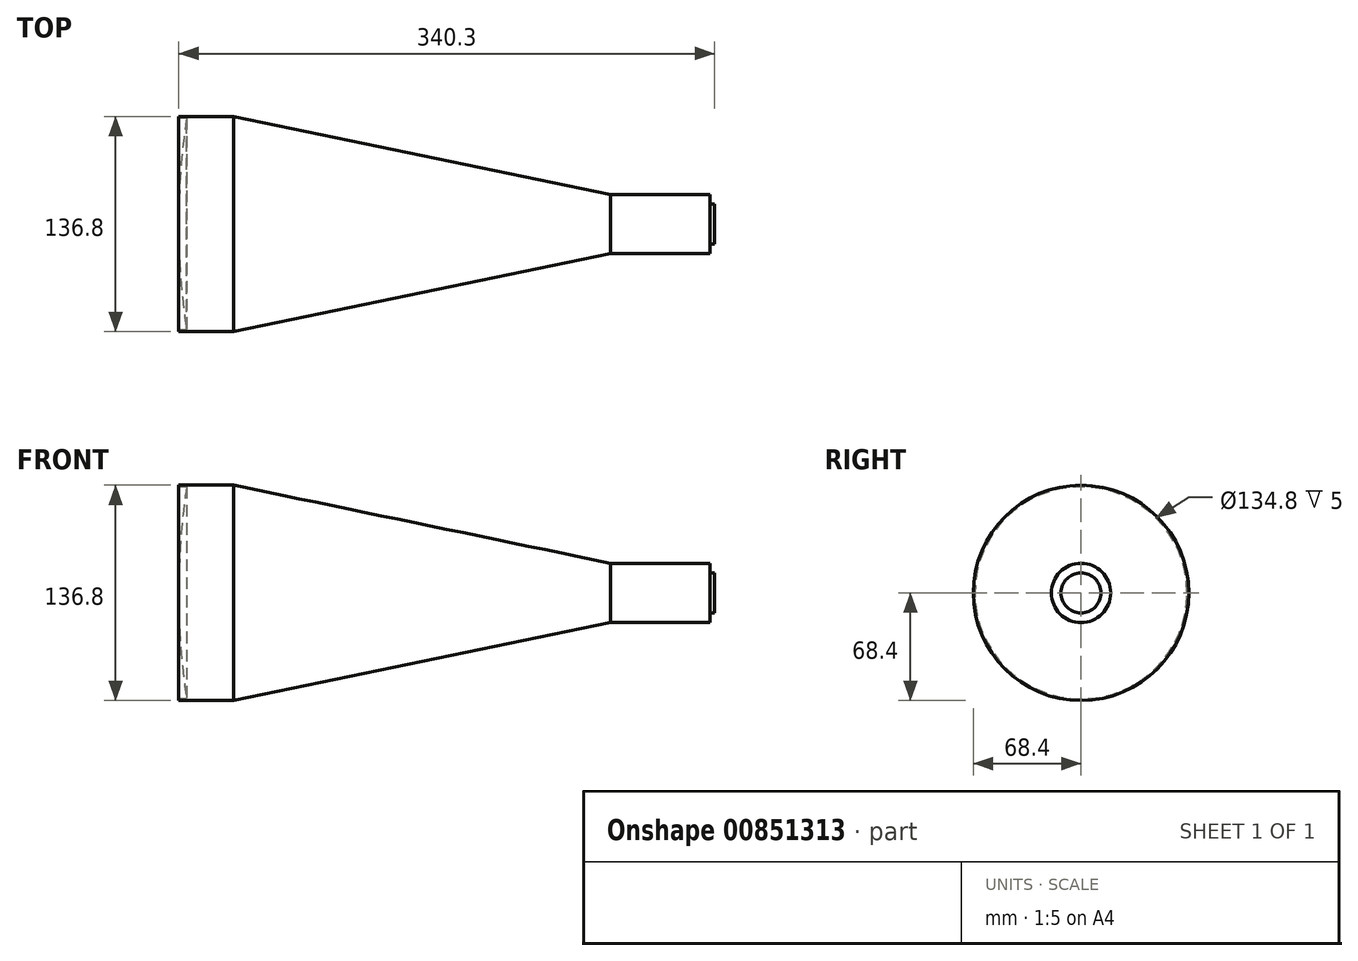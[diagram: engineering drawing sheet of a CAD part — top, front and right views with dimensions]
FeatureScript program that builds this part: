
annotation { "Feature Type Name" : "Feature", "Feature Type Description" : "" }
export const myFeature = defineFeature(function(context is Context, id is Id, definition is map)
    precondition{}
    {
        {
            var Q0;
            Q0=qCreatedBy(makeId("Front.planeOp"),FACE);
            var sketch = newSketch(context, id + "F0", { "sketchPlane" : qUnion([Q0])});
            skLineSegment(sketch, "E0", {"start": v(0, 0) * mm, "end": v(0, 12.7) * mm});
            skLineSegment(sketch, "E1", {"start": v(0, 12.7) * mm, "end": v(-3, 12.7) * mm});
            skLineSegment(sketch, "E2", {"start": v(-3, 12.7) * mm, "end": v(-3, 18.85) * mm});
            skLineSegment(sketch, "E3", {"start": v(-3, 18.85) * mm, "end": v(-66.1, 18.85) * mm});
            skLineSegment(sketch, "E4", {"start": v(-305.3, 68.4) * mm, "end": v(-340.3, 68.4) * mm});
            skLineSegment(sketch, "E5", {"start": v(-340.3, 0) * mm, "end": v(0, 0) * mm});
            skLineSegment(sketch, "E6", {"start": v(-305.3, 68.4) * mm, "end": v(-66.1, 18.85) * mm});
            skLineSegment(sketch, "E7", {"start": v(-340.3, 68.4) * mm, "end": v(-340.3, 67.4) * mm});
            skLineSegment(sketch, "E8", {"start": v(-340.3, 67.4) * mm, "end": v(-335.3, 67.4) * mm});
            skArc(sketch, "E9", {"start": v(-335.3, 67.4) * mm, "mid": v(-339.05, 33.8) * mm, "end": v(-340.3, 0) * mm});
            skSolve(sketch);
        }
        {
            var Q0;
            Q0 = qSketchRegion(id + "F0", true);
            var Q1;
            Q1=sQuery(id+"F0.wireOp",EDGE,"E5");
            revolve(context, id + "F1", {"surfaceOperationType" : NewSurfaceOperationType.NEW, "entities" : qUnion([Q0]), "axis" : qUnion([Q1]), "revolveType" : RevolveType.FULL});
        }
    });
